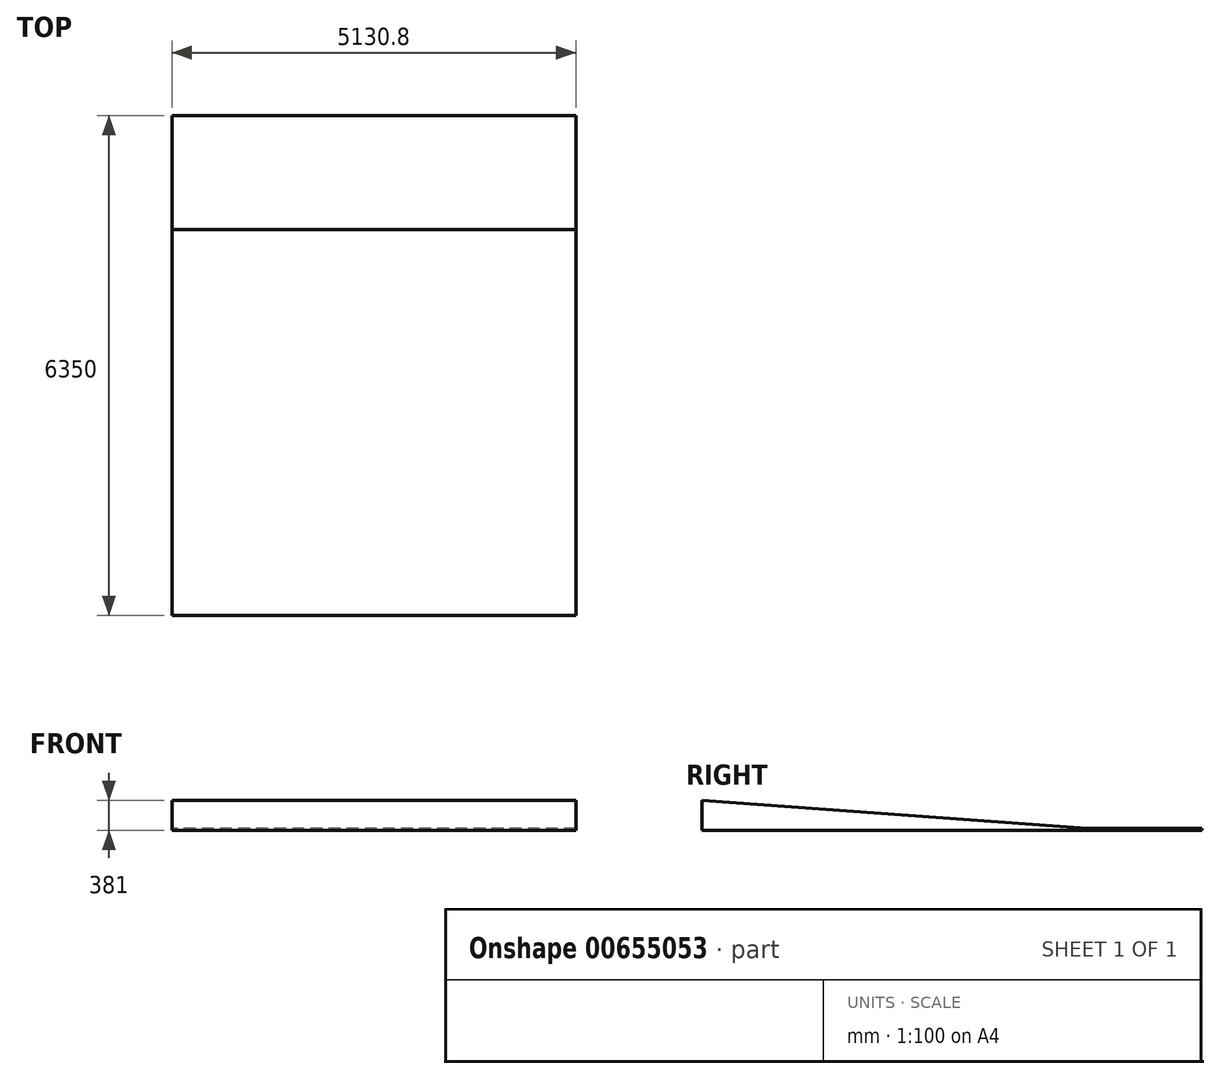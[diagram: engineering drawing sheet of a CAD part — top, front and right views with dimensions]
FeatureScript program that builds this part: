
annotation { "Feature Type Name" : "Feature", "Feature Type Description" : "" }
export const myFeature = defineFeature(function(context is Context, id is Id, definition is map)
    precondition{}
    {
        {
            var Q0;
            Q0=qCreatedBy(makeId("Top.planeOp"),FACE);
            var sketch = newSketch(context, id + "F0", { "sketchPlane" : qUnion([Q0])});
            skLineSegment(sketch, "E0.bottom", {"start": v(0, 0) * mm, "end": v(-5130.8, 0) * mm});
            skLineSegment(sketch, "E0.top", {"start": v(0, -6350) * mm, "end": v(-5130.8, -6350) * mm});
            skLineSegment(sketch, "E0.left", {"start": v(0, 0) * mm, "end": v(0, -6350) * mm});
            skLineSegment(sketch, "E0.right", {"start": v(-5130.8, 0) * mm, "end": v(-5130.8, -6350) * mm});
            skSolve(sketch);
        }
        {
            var Q0;
            Q0=makeQuery(id+"F0.imprint","IMPRINT",FACE,{"disambiguationData":[TD([[makeQuery(id+"F0.imprint","IMPRINT",EDGE,{"derivedFrom":sQuery(id+"F0.wireOp",EDGE,"E0.bottom")}),1.0]])]});
            extrude(context, id + "F1", {"entities" : qUnion([Q0]), "depth" : 25.4 * mm, "offsetDistance" : 25.4 * mm});
        }
        {
            var Q0;
            Q0=makeQuery(id+"F1.opExtrude","SWEPT_FACE",FACE,{"disambiguationData":[OSD([sQuery(id+"F0.wireOp",EDGE,"E0.right")])]});
            var sketch = newSketch(context, id + "F2", { "sketchPlane" : qUnion([Q0])});
            skLineSegment(sketch, "E1", {"start": v(6350, 25.4) * mm, "end": v(6350, 381) * mm});
            skLineSegment(sketch, "E2", {"start": v(6350, 381) * mm, "end": v(1449.8, 25.4) * mm});
            skLineSegment(sketch, "E3", {"start": v(1449.8, 25.4) * mm, "end": v(6350, 25.4) * mm});
            skSolve(sketch);
        }
        {
            var Q0;
            Q0=makeQuery(id+"F2.imprint","IMPRINT",FACE,{"disambiguationData":[TD([[makeQuery(id+"F2.imprint","IMPRINT",EDGE,{"derivedFrom":sQuery(id+"F2.wireOp",EDGE,"E1")}),1.0]])]});
            extrude(context, id + "F3", {"entities" : qUnion([Q0]), "operationType" : NewBodyOperationType.ADD, "oppositeDirection" : true, "depth" : 5130.8 * mm, "offsetDistance" : 25.4 * mm});
        }
    });
